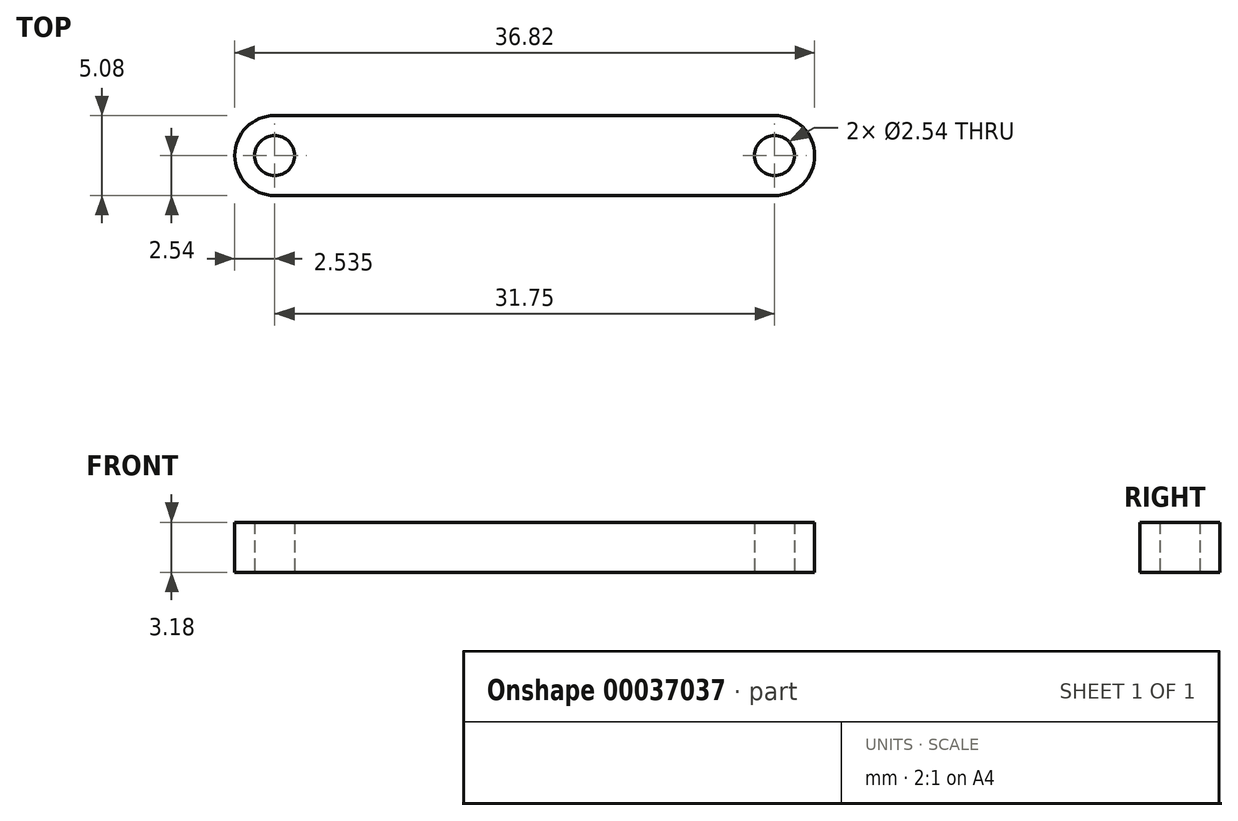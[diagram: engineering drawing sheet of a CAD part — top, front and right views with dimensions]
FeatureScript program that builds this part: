
annotation { "Feature Type Name" : "Feature", "Feature Type Description" : "" }
export const myFeature = defineFeature(function(context is Context, id is Id, definition is map)
    precondition{}
    {
        {
            var Q0;
            Q0=qCreatedBy(makeId("Top.planeOp"),FACE);
            var sketch = newSketch(context, id + "F0", { "sketchPlane" : qUnion([Q0])});
            skLineSegment(sketch, "E0.rect.bottom", {"start": v(15.88, 2.54) * mm, "end": v(-15.88, 2.54) * mm});
            skLineSegment(sketch, "E0.rect.top", {"start": v(15.88, -2.54) * mm, "end": v(-15.88, -2.54) * mm});
            skLineSegment(sketch, "E0.rect.left", {"start": v(15.88, 2.54) * mm, "end": v(15.88, -2.54) * mm});
            skLineSegment(sketch, "E0.rect.right", {"start": v(-15.88, 2.54) * mm, "end": v(-15.88, -2.54) * mm});
            skPoint(sketch, "E0.rect.middle", {"position": v(0, 0) * mm});
            skArc(sketch, "E1", {"start": v(15.88, -2.54) * mm, "mid": v(18.41, 0) * mm, "end": v(15.88, 2.54) * mm});
            skArc(sketch, "E2", {"start": v(-15.88, 2.54) * mm, "mid": v(-18.41, 0) * mm, "end": v(-15.88, -2.54) * mm});
            skCircle(sketch, "E3", {"center": v(-15.88, 0) * mm, "radius": 1.27 * mm});
            skCircle(sketch, "E4", {"center": v(15.88, 0) * mm, "radius": 1.27 * mm});
            skSolve(sketch);
        }
        {
            var Q0;
            Q0 = qSketchRegion(id + "F0", true);
            extrude(context, id + "F1", {"entities" : qUnion([Q0]), "depth" : 3.17 * mm});
        }
    });
